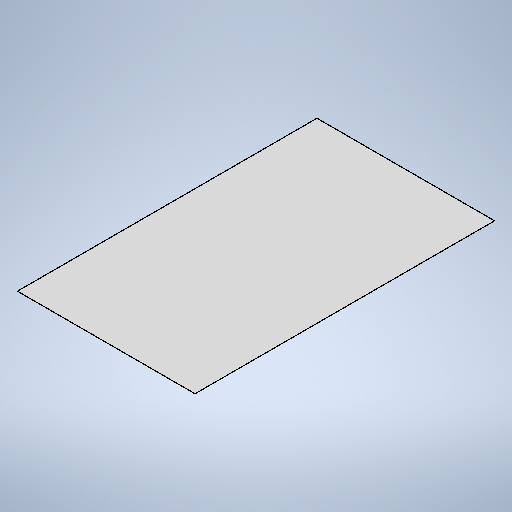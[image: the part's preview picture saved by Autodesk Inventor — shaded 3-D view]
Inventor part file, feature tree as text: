
AUTODESK INVENTOR PART (.ipt)
format: ipt  version: 2025.1 (Build 291241020, 241B)  size: 261,632 bytes
history: native  units: mm
features: other x2, sheet_metal_op x1, sketch x1
ambient origin geometry x8: Origin, YZ Plane, XZ Plane, XY Plane, X Axis, Y Axis, Z Axis, Center Point
bodies: Body1 (feature_tree)
feature tree (4):
  sheet_metal_op  "Face3"
  sketch  "Sketch1"  dims[d61=500.0mm d154=1340.0mm d155=2260.0mm d156=2.0mm]
  other  "Plate5"
  other  "Definition1"
